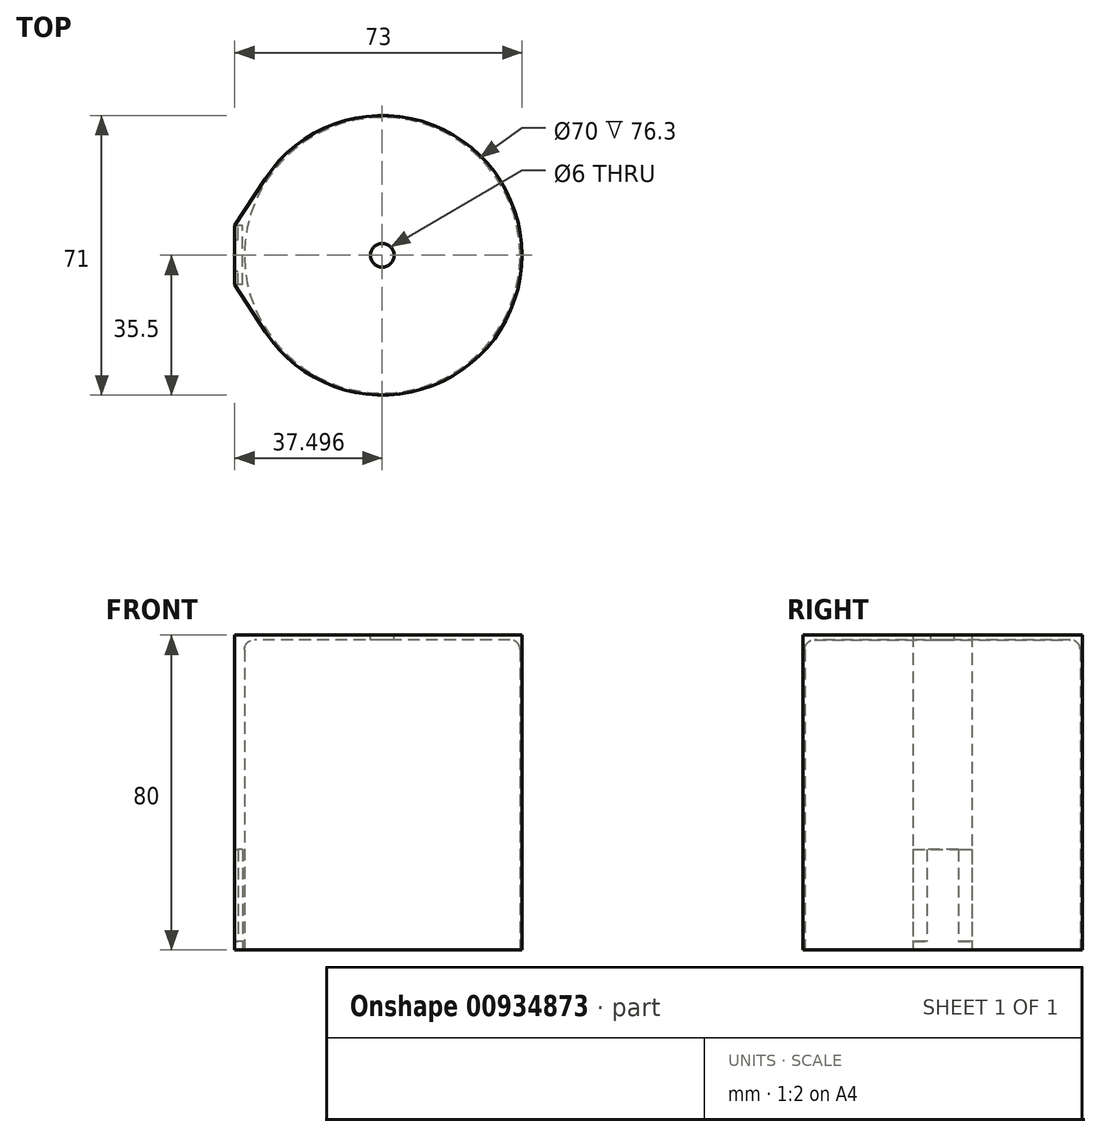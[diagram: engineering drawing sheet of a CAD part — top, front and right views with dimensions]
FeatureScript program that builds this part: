
annotation { "Feature Type Name" : "Feature", "Feature Type Description" : "" }
export const myFeature = defineFeature(function(context is Context, id is Id, definition is map)
    precondition{}
    {
        {
            var Q0;
            Q0=qCreatedBy(makeId("Top.planeOp"),FACE);
            var sketch = newSketch(context, id + "F0", { "sketchPlane" : qUnion([Q0])});
            skLineSegment(sketch, "E0", {"start": v(0, 0) * mm, "end": v(35.6, 0) * mm, "construction": true});
            skCircle(sketch, "E1", {"center": v(35.6, 0) * mm, "radius": 35.5 * mm});
            skLineSegment(sketch, "E2.0.0", {"start": v(-1.9, 7.5) * mm, "end": v(-0.1, 7.5) * mm});
            skLineSegment(sketch, "E2.0.2", {"start": v(0.1, -7.5) * mm, "end": v(-1.9, -7.5) * mm});
            skLineSegment(sketch, "E3", {"start": v(0.1, -7.5) * mm, "end": v(-1.9, -7.5) * mm, "construction": true});
            skLineSegment(sketch, "E4", {"start": v(-1.9, -7.5) * mm, "end": v(5.88, -19.4) * mm});
            skLineSegment(sketch, "E5.MirrorCS", {"start": v(-1.9, 7.5) * mm, "end": v(5.88, 19.4) * mm});
            skCircle(sketch, "E6", {"center": v(35.6, 0) * mm, "radius": 35 * mm});
            skLineSegment(sketch, "E7", {"start": v(-1.9, 7.5) * mm, "end": v(-1.9, -7.5) * mm});
            skLineSegment(sketch, "E8.bottom", {"start": v(0.1, -7.5) * mm, "end": v(-1, -7.5) * mm});
            skLineSegment(sketch, "E8.top", {"start": v(0.1, 7.5) * mm, "end": v(-1, 7.5) * mm});
            skLineSegment(sketch, "E8.left", {"start": v(0.1, -7.5) * mm, "end": v(0.1, 7.5) * mm});
            skLineSegment(sketch, "E8.right", {"start": v(-1, -7.5) * mm, "end": v(-1, 7.5) * mm});
            skLineSegment(sketch, "E9", {"start": v(-1, 0) * mm, "end": v(-1, -4) * mm, "construction": true});
            skLineSegment(sketch, "E10.bottom", {"start": v(-1.9, -4) * mm, "end": v(-0.1, -4) * mm});
            skLineSegment(sketch, "E10.top", {"start": v(-1.9, 4) * mm, "end": v(-0.1, 4) * mm});
            skLineSegment(sketch, "E10.left", {"start": v(-1.9, -4) * mm, "end": v(-1.9, 4) * mm});
            skLineSegment(sketch, "E10.right", {"start": v(-0.1, -4) * mm, "end": v(-0.1, 4) * mm});
            skSolve(sketch);
        }
        {
            var Q0;
            Q0=makeQuery(id+"F0.imprint","IMPRINT",FACE,{"disambiguationData":[TD([[makeQuery(id+"F0.imprint","IMPRINT",EDGE,{"derivedFrom":sQuery(id+"F0.wireOp",EDGE,"E6")}),-1.0]])]});
            var Q1;
            {var subQ4=sQuery(id+"F0.wireOp",EDGE,"E2.0.2");Q1=makeQuery(id+"F0.imprint","IMPRINT",FACE,{"disambiguationData":[TD([[makeQuery(id+"F0.imprint","IMPRINT",EDGE,{"derivedFrom":subQ4}),1.0]])]});}
            var Q2;
            {var subQ1=sQuery(id+"F0.wireOp",EDGE,"E5.MirrorCS");Q2=makeQuery(id+"F0.imprint","IMPRINT",FACE,{"disambiguationData":[TD([[makeQuery(id+"F0.imprint","IMPRINT",EDGE,{"derivedFrom":subQ1}),-1.0]])]});}
            var Q3;
            Q3=makeQuery(id+"F0.imprint","IMPRINT",FACE,{"disambiguationData":[TD([[makeQuery(id+"F0.imprint","IMPRINT",EDGE,{"derivedFrom":sQuery(id+"F0.wireOp",EDGE,"E6")}),1.0]])]});
            var Q4;
            {var subQ3=sQuery(id+"F0.wireOp",EDGE,"E7");var subQ5=sQuery(id+"F0.wireOp",EDGE,"E10.top");var subQ6=makeQuery(id+"F0.imprint","INTERSECT",VERTEX,{"derivedFrom":[subQ3,subQ5]});Q4=makeQuery(id+"F0.imprint","IMPRINT",FACE,{"disambiguationData":[TD([[makeQuery(id+"F0.imprint","IMPRINT",EDGE,{"disambiguationData":[TD([[subQ6,-1.0]])],"derivedFrom":subQ5}),1.0]])]});}
            var Q5;
            {var subQ5=sQuery(id+"F0.wireOp",EDGE,"E2.0.2");Q5=makeQuery(id+"F0.imprint","IMPRINT",FACE,{"disambiguationData":[TD([[makeQuery(id+"F0.imprint","IMPRINT",EDGE,{"derivedFrom":subQ5}),-1.0]])]});}
            var Q6;
            {var subQ1=sQuery(id+"F0.wireOp",EDGE,"E8.bottom");Q6=makeQuery(id+"F0.imprint","IMPRINT",FACE,{"disambiguationData":[TD([[makeQuery(id+"F0.imprint","IMPRINT",EDGE,{"derivedFrom":subQ1}),-1.0]])]});}
            var Q7;
            {var subQ5=sQuery(id+"F0.wireOp",EDGE,"E10.right");Q7=makeQuery(id+"F0.imprint","IMPRINT",FACE,{"disambiguationData":[TD([[makeQuery(id+"F0.imprint","IMPRINT",EDGE,{"derivedFrom":subQ5}),1.0]])]});}
            var Q8;
            {var subQ1=sQuery(id+"F0.wireOp",EDGE,"E8.bottom");Q8=makeQuery(id+"F0.imprint","IMPRINT",FACE,{"disambiguationData":[TD([[makeQuery(id+"F0.imprint","IMPRINT",EDGE,{"derivedFrom":subQ1}),-1.0]])]});}
            var Q9;
            {var subQ0=sQuery(id+"F0.wireOp",EDGE,"E10.top");var subQ1=sQuery(id+"F0.wireOp",EDGE,"E7");var subQ2=makeQuery(id+"F0.imprint","INTERSECT",VERTEX,{"derivedFrom":[subQ1,subQ0]});Q9=makeQuery(id+"F0.imprint","IMPRINT",FACE,{"disambiguationData":[TD([[makeQuery(id+"F0.imprint","IMPRINT",EDGE,{"disambiguationData":[TD([[subQ2,-1.0]])],"derivedFrom":subQ1}),1.0]])]});}
            var Q10;
            {var subQ1=sQuery(id+"F0.wireOp",EDGE,"E8.bottom");Q10=makeQuery(id+"F0.imprint","IMPRINT",FACE,{"disambiguationData":[TD([[makeQuery(id+"F0.imprint","IMPRINT",EDGE,{"derivedFrom":subQ1}),-1.0]])]});}
            var Q11;
            {var subQ0=sQuery(id+"F0.wireOp",EDGE,"E10.top");var subQ1=sQuery(id+"F0.wireOp",EDGE,"E7");var subQ2=makeQuery(id+"F0.imprint","INTERSECT",VERTEX,{"derivedFrom":[subQ1,subQ0]});var subQ8=makeQuery(id+"F0.imprint","IMPRINT",EDGE,{"disambiguationData":[TD([[subQ2,-1.0]])],"derivedFrom":subQ0});Q11=qUnion([makeQuery(id+"F0.imprint","IMPRINT",FACE,{"disambiguationData":[TD([[subQ8,1.0]])]}),makeQuery(id+"F0.imprint","IMPRINT",FACE,{"disambiguationData":[TD([[makeQuery(id+"F0.imprint","IMPRINT",EDGE,{"disambiguationData":[TD([[subQ2,-1.0]])],"derivedFrom":subQ1}),1.0]])]})]);}
            extrude(context, id + "F1", {"entities" : qUnion([Q0, Q1, Q2, Q3, Q4, Q5, Q6, Q7, Q8, Q9, Q10, Q11]), "depth" : 80 * mm, "offsetDistance" : 25 * mm});
        }
        {
            var Q0;
            Q0=makeQuery(id+"F0.imprint","IMPRINT",FACE,{"disambiguationData":[TD([[makeQuery(id+"F0.imprint","IMPRINT",EDGE,{"derivedFrom":sQuery(id+"F0.wireOp",EDGE,"E6")}),1.0]])]});
            extrude(context, id + "F2", {"entities" : qUnion([Q0]), "operationType" : NewBodyOperationType.REMOVE, "depth" : 78.8 * mm, "offsetDistance" : 25 * mm});
        }
        {
            var Q0;
            {var subQ5=sQuery(id+"F0.wireOp",EDGE,"E10.right");Q0=makeQuery(id+"F0.imprint","IMPRINT",FACE,{"disambiguationData":[TD([[makeQuery(id+"F0.imprint","IMPRINT",EDGE,{"derivedFrom":subQ5}),1.0]])]});}
            var Q1;
            {var subQ1=sQuery(id+"F0.wireOp",EDGE,"E8.bottom");Q1=makeQuery(id+"F0.imprint","IMPRINT",FACE,{"disambiguationData":[TD([[makeQuery(id+"F0.imprint","IMPRINT",EDGE,{"derivedFrom":subQ1}),-1.0]])]});}
            var Q2;
            {var subQ0=sQuery(id+"F0.wireOp",EDGE,"E10.top");var subQ1=sQuery(id+"F0.wireOp",EDGE,"E7");var subQ2=makeQuery(id+"F0.imprint","INTERSECT",VERTEX,{"derivedFrom":[subQ1,subQ0]});Q2=makeQuery(id+"F0.imprint","IMPRINT",FACE,{"disambiguationData":[TD([[makeQuery(id+"F0.imprint","IMPRINT",EDGE,{"disambiguationData":[TD([[subQ2,-1.0]])],"derivedFrom":subQ1}),1.0]])]});}
            var Q3;
            {var subQ1=sQuery(id+"F0.wireOp",EDGE,"E8.bottom");Q3=makeQuery(id+"F0.imprint","IMPRINT",FACE,{"disambiguationData":[TD([[makeQuery(id+"F0.imprint","IMPRINT",EDGE,{"derivedFrom":subQ1}),-1.0]])]});}
            var Q4;
            {var subQ1=sQuery(id+"F0.wireOp",EDGE,"E8.bottom");Q4=makeQuery(id+"F0.imprint","IMPRINT",FACE,{"disambiguationData":[TD([[makeQuery(id+"F0.imprint","IMPRINT",EDGE,{"derivedFrom":subQ1}),-1.0]])]});}
            var Q5;
            {var subQ0=sQuery(id+"F0.wireOp",EDGE,"E10.top");var subQ1=sQuery(id+"F0.wireOp",EDGE,"E7");var subQ2=makeQuery(id+"F0.imprint","INTERSECT",VERTEX,{"derivedFrom":[subQ1,subQ0]});Q5=makeQuery(id+"F0.imprint","IMPRINT",FACE,{"disambiguationData":[TD([[makeQuery(id+"F0.imprint","IMPRINT",EDGE,{"disambiguationData":[TD([[subQ2,-1.0]])],"derivedFrom":subQ1}),1.0]])]});}
            extrude(context, id + "F3", {"entities" : qUnion([Q0, Q1, Q2, Q3, Q4, Q5]), "operationType" : NewBodyOperationType.REMOVE, "depth" : 37 * mm, "offsetDistance" : 25 * mm});
        }
        {
            var Q0;
            Q0=makeQuery(id+"F1.opExtrude","CAP_FACE",FACE,{"disambiguationData":[OSD([sQuery(id+"F0.wireOp",EDGE,"E1"),sQuery(id+"F0.wireOp",EDGE,"E4"),sQuery(id+"F0.wireOp",EDGE,"E5.MirrorCS"),sQuery(id+"F0.wireOp",EDGE,"E7")])],"isStart":false});
            var sketch = newSketch(context, id + "F4", { "sketchPlane" : qUnion([Q0])});
            skPoint(sketch, "E11", {"position": v(35.6, 0) * mm});
            skSolve(sketch);
        }
        {
            var Q0;
            Q0=sQuery(id+"F4.wireOp",VERTEX,"E11");
            var Q1;
            Q1=makeQuery(id+"F1.opExtrude","SWEPT_BODY",BODY,{"disambiguationData":[OSD([sQuery(id+"F0.wireOp",EDGE,"E1"),sQuery(id+"F0.wireOp",EDGE,"E4"),sQuery(id+"F0.wireOp",EDGE,"E5.MirrorCS"),sQuery(id+"F0.wireOp",EDGE,"E7")])]});
            hole(context, id + "F5", {"style" : HoleStyle.SIMPLE, "endStyle" : HoleEndStyle.THROUGH, "holeDiameter" : 6 * mm, "majorDiameter" : 5 * mm, "isTappedThrough" : true, "tappedDepth" : 12 * mm, "tapClearance" : 3, "startFromSketch" : true, "locations" : qUnion([Q0]), "scope" : qUnion([Q1])});
        }
        {
            var Q0;
            {var subQ5=sQuery(id+"F0.wireOp",EDGE,"E2.0.2");Q0=makeQuery(id+"F0.imprint","IMPRINT",FACE,{"disambiguationData":[TD([[makeQuery(id+"F0.imprint","IMPRINT",EDGE,{"derivedFrom":subQ5}),-1.0]])]});}
            var Q1;
            {var subQ3=sQuery(id+"F0.wireOp",EDGE,"E7");var subQ5=sQuery(id+"F0.wireOp",EDGE,"E10.top");var subQ6=makeQuery(id+"F0.imprint","INTERSECT",VERTEX,{"derivedFrom":[subQ3,subQ5]});Q1=makeQuery(id+"F0.imprint","IMPRINT",FACE,{"disambiguationData":[TD([[makeQuery(id+"F0.imprint","IMPRINT",EDGE,{"disambiguationData":[TD([[subQ6,-1.0]])],"derivedFrom":subQ5}),1.0]])]});}
            extrude(context, id + "F6", {"entities" : qUnion([Q0, Q1]), "operationType" : NewBodyOperationType.REMOVE, "depth" : 2.2 * mm, "offsetDistance" : 25 * mm});
        }
        {
            var Q0;
            Q0=makeQuery(id+"F3.boolean.opBoolean","COPY",FACE,{"derivedFrom":makeQuery(id+"F3.opExtrude","CAP_FACE",FACE,{"disambiguationData":[OSD([sQuery(id+"F0.wireOp",EDGE,"E7"),sQuery(id+"F0.wireOp",EDGE,"E8.bottom"),sQuery(id+"F0.wireOp",EDGE,"E8.top"),sQuery(id+"F0.wireOp",EDGE,"E8.left"),sQuery(id+"F0.wireOp",EDGE,"E8.right"),sQuery(id+"F0.wireOp",EDGE,"E10.bottom"),sQuery(id+"F0.wireOp",EDGE,"E10.top")])],"isStart":false})});
            extrude(context, id + "F7", {"entities" : qUnion([Q0]), "operationType" : NewBodyOperationType.ADD, "depth" : 11.5 * mm, "offsetDistance" : 25 * mm});
        }
        {
            var Q0;
            Q0=makeQuery(id+"F2.boolean.opBoolean","COPY",EDGE,{"derivedFrom":makeQuery(id+"F2.opExtrude","CAP_EDGE",EDGE,{"disambiguationData":[OSD([sQuery(id+"F0.wireOp",EDGE,"E6")])],"isStart":false})});
            fillet(context, id + "F8", {"entities" : qUnion([Q0]), "radius" : 2.5 * mm, "tangentPropagation" : true, "allowEdgeOverflow" : false});
        }
    });
